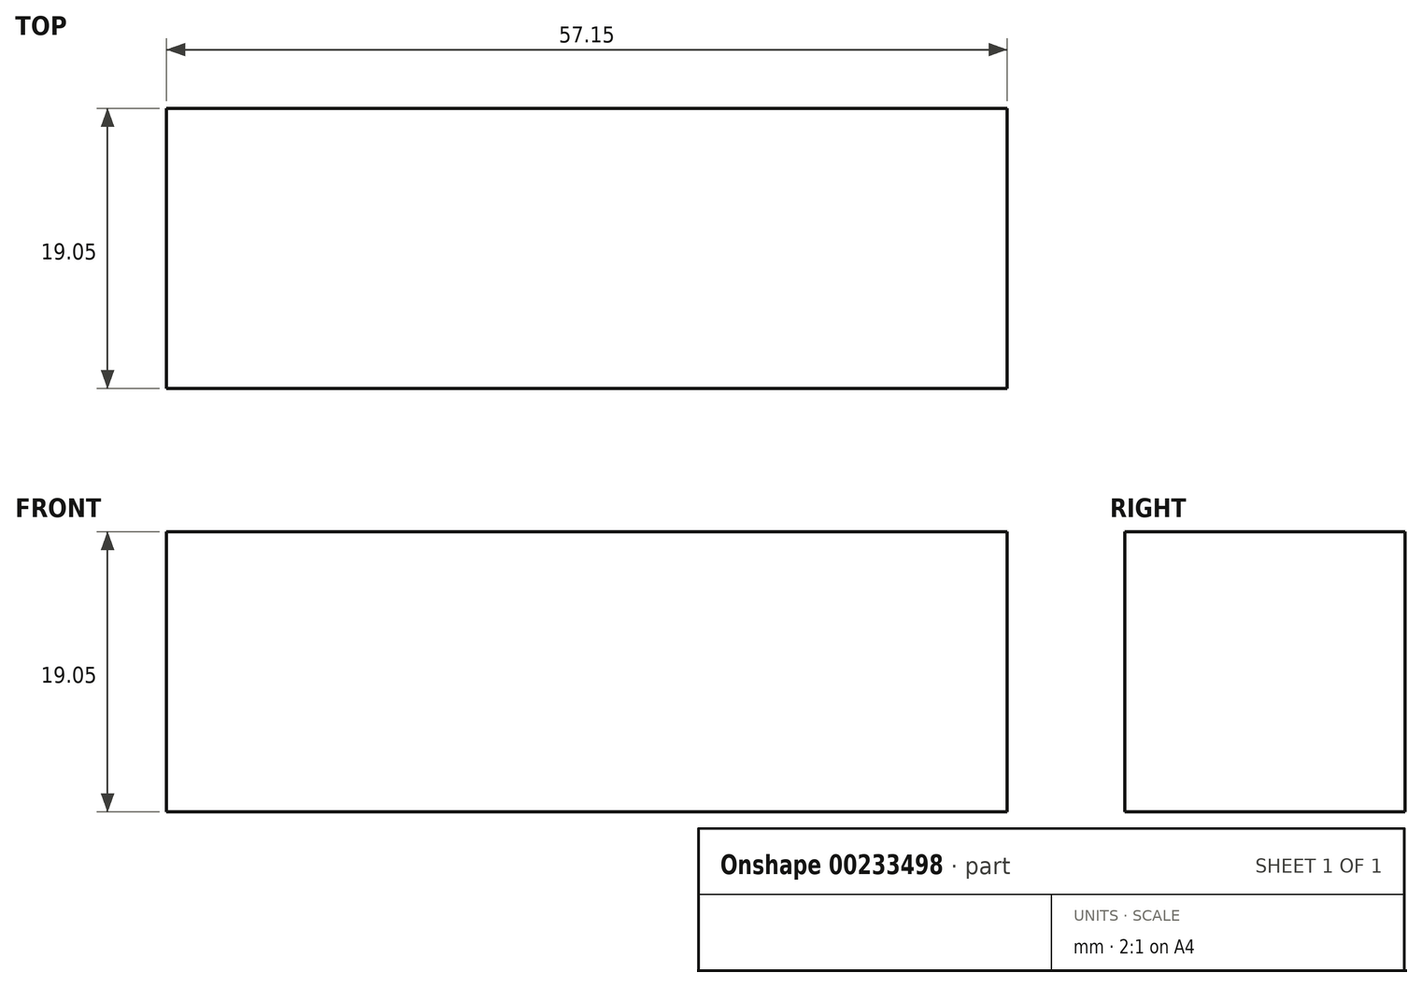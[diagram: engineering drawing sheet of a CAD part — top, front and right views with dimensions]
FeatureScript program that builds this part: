
annotation { "Feature Type Name" : "Feature", "Feature Type Description" : "" }
export const myFeature = defineFeature(function(context is Context, id is Id, definition is map)
    precondition{}
    {
        {
            var Q0;
            Q0=qCreatedBy(makeId("Front.planeOp"),FACE);
            var sketch = newSketch(context, id + "F0", { "sketchPlane" : qUnion([Q0])});
            skLineSegment(sketch, "E0.bottom", {"start": v(77.75, -48.02) * mm, "end": v(134.9, -48.02) * mm});
            skLineSegment(sketch, "E0.top", {"start": v(77.75, -67.07) * mm, "end": v(134.9, -67.07) * mm});
            skLineSegment(sketch, "E0.left", {"start": v(77.75, -48.02) * mm, "end": v(77.75, -67.07) * mm});
            skLineSegment(sketch, "E0.right", {"start": v(134.9, -48.02) * mm, "end": v(134.9, -67.07) * mm});
            skSolve(sketch);
        }
        {
            var Q0;
            Q0=makeQuery(id+"F0.imprint","IMPRINT",FACE,{"disambiguationData":[TD([[makeQuery(id+"F0.imprint","IMPRINT",EDGE,{"derivedFrom":sQuery(id+"F0.wireOp",EDGE,"E0.bottom")}),-1.0]])]});
            extrude(context, id + "F1", {"entities" : qUnion([Q0]), "depth" : 19.05 * mm});
        }
    });
